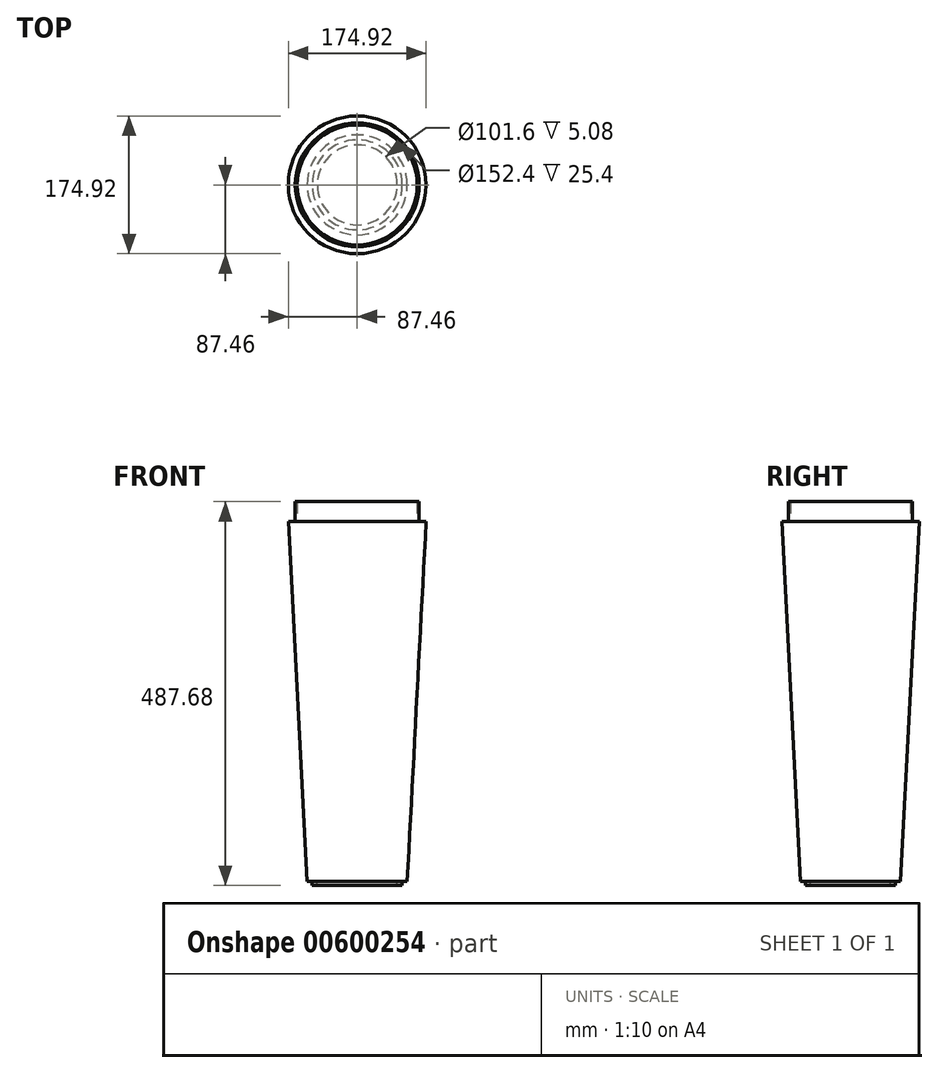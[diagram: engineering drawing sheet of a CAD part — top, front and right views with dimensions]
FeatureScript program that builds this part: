
annotation { "Feature Type Name" : "Feature", "Feature Type Description" : "" }
export const myFeature = defineFeature(function(context is Context, id is Id, definition is map)
    precondition{}
    {
        {
            var Q0;
            Q0=qCreatedBy(makeId("Top.planeOp"),FACE);
            var sketch = newSketch(context, id + "F0", { "sketchPlane" : qUnion([Q0])});
            skCircle(sketch, "E0", {"center": v(0, 0) * mm, "radius": 63.5 * mm});
            skSolve(sketch);
        }
        {
            var Q0;
            Q0=makeQuery(id+"F0.imprint","IMPRINT",FACE,{"disambiguationData":[TD([[makeQuery(id+"F0.imprint","IMPRINT",EDGE,{"derivedFrom":sQuery(id+"F0.wireOp",EDGE,"E0")}),1.0]])]});
            extrude(context, id + "F1", {"entities" : qUnion([Q0]), "depth" : 457.2 * mm, "offsetDistance" : 25.4 * mm, "hasDraft" : true, "draftAngle" : 3 * degree});
        }
        {
            var Q0;
            Q0=makeQuery(id+"F1.opExtrude","CAP_FACE",FACE,{"disambiguationData":[OSD([sQuery(id+"F0.wireOp",EDGE,"E0")])],"isStart":true});
            var sketch = newSketch(context, id + "F2", { "sketchPlane" : qUnion([Q0])});
            skCircle(sketch, "E1", {"center": v(0, 0) * mm, "radius": 50.8 * mm});
            skCircle(sketch, "E2", {"center": v(0, 0) * mm, "radius": 57.15 * mm});
            skSolve(sketch);
        }
        {
            var Q0;
            Q0=makeQuery(id+"F2.imprint","IMPRINT",FACE,{"disambiguationData":[TD([[makeQuery(id+"F2.imprint","IMPRINT",EDGE,{"derivedFrom":sQuery(id+"F2.wireOp",EDGE,"E1")}),-1.0]])]});
            extrude(context, id + "F3", {"entities" : qUnion([Q0]), "operationType" : NewBodyOperationType.ADD, "depth" : 5.08 * mm, "offsetDistance" : 25.4 * mm});
        }
        {
            var Q0;
            Q0=makeQuery(id+"F1.opExtrude","CAP_FACE",FACE,{"disambiguationData":[OSD([sQuery(id+"F0.wireOp",EDGE,"E0")])],"isStart":false});
            var sketch = newSketch(context, id + "F4", { "sketchPlane" : qUnion([Q0])});
            skCircle(sketch, "E3", {"center": v(0, 0) * mm, "radius": 76.2 * mm});
            skCircle(sketch, "E4", {"center": v(0, 0) * mm, "radius": 78.74 * mm});
            skSolve(sketch);
        }
        {
            var Q0;
            Q0 = qSketchRegion(id + "F4", true);
            extrude(context, id + "F5", {"entities" : qUnion([Q0]), "operationType" : NewBodyOperationType.ADD, "depth" : 25.4 * mm, "offsetDistance" : 25.4 * mm});
        }
    });
